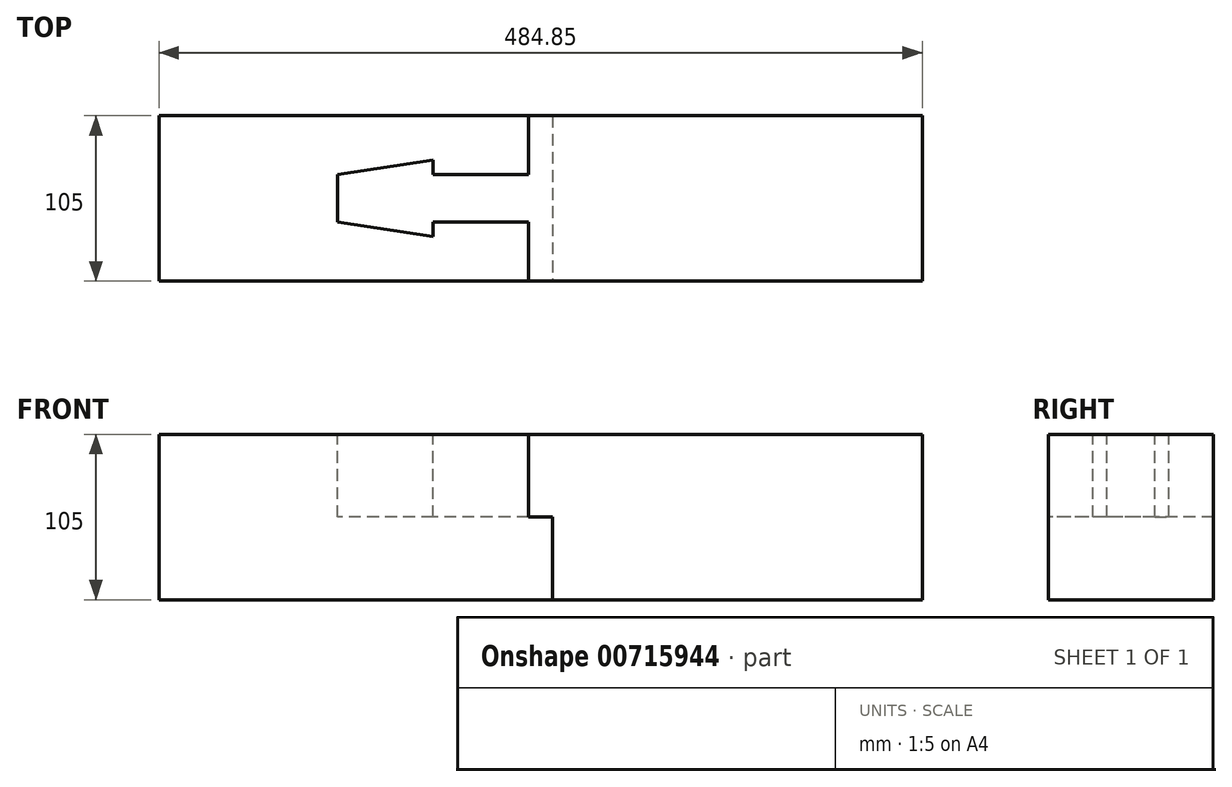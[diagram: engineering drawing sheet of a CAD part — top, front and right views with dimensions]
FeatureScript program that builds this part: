
annotation { "Feature Type Name" : "Feature", "Feature Type Description" : "" }
export const myFeature = defineFeature(function(context is Context, id is Id, definition is map)
    precondition{}
    {
        {
            var Q0;
            Q0=qCreatedBy(makeId("Top.planeOp"),FACE);
            var sketch = newSketch(context, id + "F0", { "sketchPlane" : qUnion([Q0])});
            skLineSegment(sketch, "E0.bottom", {"start": v(0, 52.5) * mm, "end": v(250, 52.5) * mm});
            skLineSegment(sketch, "E0.top", {"start": v(0, -52.5) * mm, "end": v(250, -52.5) * mm});
            skLineSegment(sketch, "E0.left", {"start": v(0, 52.5) * mm, "end": v(0, -52.5) * mm});
            skLineSegment(sketch, "E0.right", {"start": v(250, 52.5) * mm, "end": v(250, -52.5) * mm});
            skSolve(sketch);
        }
        {
            var Q0;
            Q0=makeQuery(id+"F0.imprint","IMPRINT",FACE,{"disambiguationData":[TD([[makeQuery(id+"F0.imprint","IMPRINT",EDGE,{"derivedFrom":sQuery(id+"F0.wireOp",EDGE,"E0.bottom")}),-1.0]])]});
            extrude(context, id + "F1", {"entities" : qUnion([Q0]), "depth" : 105 * mm, "offsetDistance" : 25 * mm, "symmetric" : true});
        }
        {
            var Q0;
            Q0=makeQuery(id+"F1.opExtrude","SWEPT_FACE",FACE,{"disambiguationData":[OSD([sQuery(id+"F0.wireOp",EDGE,"E0.left")])]});
            var sketch = newSketch(context, id + "F2", { "sketchPlane" : qUnion([Q0])});
            skLineSegment(sketch, "E1.bottom", {"start": v(-52.5, -52.5) * mm, "end": v(52.5, -52.5) * mm});
            skLineSegment(sketch, "E1.top", {"start": v(-52.5, 0) * mm, "end": v(52.5, 0) * mm});
            skLineSegment(sketch, "E1.left", {"start": v(-52.5, -52.5) * mm, "end": v(-52.5, 0) * mm});
            skLineSegment(sketch, "E1.right", {"start": v(52.5, -52.5) * mm, "end": v(52.5, 0) * mm});
            skSolve(sketch);
        }
        {
            var Q0;
            Q0=makeQuery(id+"F2.imprint","IMPRINT",FACE,{"disambiguationData":[TD([[makeQuery(id+"F2.imprint","IMPRINT",EDGE,{"derivedFrom":sQuery(id+"F2.wireOp",EDGE,"E1.bottom")}),1.0]])]});
            extrude(context, id + "F3", {"entities" : qUnion([Q0]), "operationType" : NewBodyOperationType.REMOVE, "oppositeDirection" : true, "depth" : 15.15 * mm, "offsetDistance" : 25 * mm});
        }
        {
            var Q0;
            Q0=makeQuery(id+"F1.opExtrude","CAP_FACE",FACE,{"disambiguationData":[OSD([sQuery(id+"F0.wireOp",EDGE,"E0.bottom"),sQuery(id+"F0.wireOp",EDGE,"E0.top"),sQuery(id+"F0.wireOp",EDGE,"E0.left"),sQuery(id+"F0.wireOp",EDGE,"E0.right")])],"isStart":false});
            var sketch = newSketch(context, id + "F4", { "sketchPlane" : qUnion([Q0])});
            skLineSegment(sketch, "E2", {"start": v(0, 15.15) * mm, "end": v(-60.6, 15.15) * mm});
            skLineSegment(sketch, "E3", {"start": v(-60.6, 15.15) * mm, "end": v(-60.6, 24.24) * mm});
            skLineSegment(sketch, "E4", {"start": v(-60.6, 24.24) * mm, "end": v(-121.2, 15.15) * mm});
            skLineSegment(sketch, "E5", {"start": v(-121.2, 15.15) * mm, "end": v(-121.2, -15.15) * mm});
            skLineSegment(sketch, "E6", {"start": v(-121.2, -15.15) * mm, "end": v(-60.6, -24.24) * mm});
            skLineSegment(sketch, "E7", {"start": v(-60.6, -24.24) * mm, "end": v(-60.6, -15.15) * mm});
            skLineSegment(sketch, "E8", {"start": v(-60.6, -15.15) * mm, "end": v(0, -15.15) * mm});
            skSolve(sketch);
        }
        {
            var Q0;
            {var subQ0=sQuery(id+"F4.wireOp",EDGE,"E2");Q0=makeQuery(id+"F4.imprint","IMPRINT",FACE,{"disambiguationData":[TD([[makeQuery(id+"F4.imprint","IMPRINT",EDGE,{"derivedFrom":subQ0}),1.0]])]});}
            var Q1;
            Q1=makeQuery(id+"F3.boolean.opBoolean","COPY",FACE,{"derivedFrom":makeQuery(id+"F3.opExtrude","SWEPT_FACE",FACE,{"disambiguationData":[OSD([sQuery(id+"F2.wireOp",EDGE,"E1.top")])]})});
            extrude(context, id + "F5", {"entities" : qUnion([Q0]), "operationType" : NewBodyOperationType.ADD, "endBound" : BoundingType.UP_TO_SURFACE, "oppositeDirection" : true, "depth" : 25 * mm, "endBoundEntityFace" : qUnion([Q1]), "offsetDistance" : 25 * mm});
        }
        {
            var Q0;
            Q0=qCreatedBy(makeId("Top.planeOp"),FACE);
            var sketch = newSketch(context, id + "F6", { "sketchPlane" : qUnion([Q0])});
            skLineSegment(sketch, "E9.0", {"start": v(15.15, 52.5) * mm, "end": v(15.15, -52.5) * mm});
            skLineSegment(sketch, "E10", {"start": v(15.15, 52.5) * mm, "end": v(-234.85, 52.5) * mm});
            skLineSegment(sketch, "E11", {"start": v(-234.85, 52.5) * mm, "end": v(-234.85, -52.5) * mm});
            skLineSegment(sketch, "E12", {"start": v(-234.85, -52.5) * mm, "end": v(15.15, -52.5) * mm});
            skSolve(sketch);
        }
        {
            var Q0;
            Q0=makeQuery(id+"F6.imprint","IMPRINT",FACE,{"disambiguationData":[TD([[makeQuery(id+"F6.imprint","IMPRINT",EDGE,{"derivedFrom":sQuery(id+"F6.wireOp",EDGE,"E9.0")}),-1.0]])]});
            var Q1;
            {var subQ0=sQuery(id+"F0.wireOp",EDGE,"E0.left");Q1=makeQuery(id+"F5.boolean.opBoolean","MERGE",FACE,{"derivedFrom":[makeQuery(id+"F1.opExtrude","CAP_FACE",FACE,{"disambiguationData":[OSD([sQuery(id+"F0.wireOp",EDGE,"E0.bottom"),sQuery(id+"F0.wireOp",EDGE,"E0.top"),subQ0,sQuery(id+"F0.wireOp",EDGE,"E0.right")])],"isStart":false}),makeQuery(id+"F5.opExtrude","CAP_FACE",FACE,{"disambiguationData":[OSD([subQ0,sQuery(id+"F4.wireOp",EDGE,"E2"),sQuery(id+"F4.wireOp",EDGE,"E3"),sQuery(id+"F4.wireOp",EDGE,"E4"),sQuery(id+"F4.wireOp",EDGE,"E5"),sQuery(id+"F4.wireOp",EDGE,"E6"),sQuery(id+"F4.wireOp",EDGE,"E7"),sQuery(id+"F4.wireOp",EDGE,"E8")])],"isStart":true})]});}
            var Q2;
            Q2=makeQuery(id+"F1.opExtrude","CAP_FACE",FACE,{"disambiguationData":[OSD([sQuery(id+"F0.wireOp",EDGE,"E0.bottom"),sQuery(id+"F0.wireOp",EDGE,"E0.top"),sQuery(id+"F0.wireOp",EDGE,"E0.left"),sQuery(id+"F0.wireOp",EDGE,"E0.right")])],"isStart":true});
            extrude(context, id + "F7", {"entities" : qUnion([Q0]), "endBound" : BoundingType.UP_TO_SURFACE, "depth" : 25 * mm, "endBoundEntityFace" : qUnion([Q1]), "offsetDistance" : 25 * mm, "hasSecondDirection" : true, "secondDirectionBound" : BoundingType.UP_TO_SURFACE, "secondDirectionOppositeDirection" : true, "secondDirectionDepth" : 25 * mm, "secondDirectionBoundEntityFace" : qUnion([Q2])});
        }
        {
            var Q0;
            Q0=makeQuery(id+"F1.opExtrude","SWEPT_BODY",BODY,{"disambiguationData":[OSD([sQuery(id+"F0.wireOp",EDGE,"E0.bottom"),sQuery(id+"F0.wireOp",EDGE,"E0.top"),sQuery(id+"F0.wireOp",EDGE,"E0.left"),sQuery(id+"F0.wireOp",EDGE,"E0.right")])]});
            var Q1;
            Q1=makeQuery(id+"F7.opExtrude","SWEPT_BODY",BODY,{"disambiguationData":[OSD([sQuery(id+"F6.wireOp",EDGE,"E9.0"),sQuery(id+"F6.wireOp",EDGE,"E10"),sQuery(id+"F6.wireOp",EDGE,"E11"),sQuery(id+"F6.wireOp",EDGE,"E12")])]});
            booleanBodies(context, id + "F8", {"operationType" : BooleanOperationType.SUBTRACTION, "tools" : qUnion([Q0]), "targets" : qUnion([Q1]), "keepTools" : true});
        }
    });
